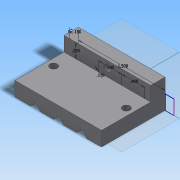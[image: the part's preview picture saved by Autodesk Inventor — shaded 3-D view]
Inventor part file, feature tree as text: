
AUTODESK INVENTOR PART (.ipt)
format: ipt  version: 2014 SP2 (Build 180246200, 246)  size: 177,664 bytes
history: native  units: in
note: dims shown in document units (in); Inventor stores cm internally (conversion verified against a paired STEP export)
features: sketch x6, extrude x6, other x3, hole x2, mirror x1
ambient origin geometry x8: Origin, YZ Plane, XZ Plane, XY Plane, X Axis, Y Axis, Z Axis, Center Point
bodies: Solid1 (feature_tree)
feature tree (18):
  other  "Table"
  other  "keyhole holder-01"
  other  "keyhole holder-02"
  sketch  "Sketch1"  dims[d0=0.1775in d3=0.4in]
  extrude  "Extrusion1"  Depth=0.4in
  extrude  "Extrusion2"  Depth=0.25in
  extrude  "Extrusion3"  Depth=1.1in TaperAngle=0.0deg
  hole  "Hole1"  [1 undecoded]
  mirror  "Mirror1"
  sketch  "Sketch7"  dims[d9=0.81in d10=0.0in d11=0.16in]
  extrude  "Extrusion5"  Depth=0.25in TaperAngle=0.0deg
  hole  "Hole2"  [1 undecoded]
  extrude  "Extrusion6"  Depth=0.25in
  extrude  "Extrusion7"  Depth=0.25in
  sketch  "Sketch2"  dims[d4=0.4in d5=0.25in]
  sketch  "Sketch3"  dims[d6=1.5in d7=1.1in d8=0.0in]
  sketch  "Sketch8"  dims[d12=0.19in d13=0.0in]
  sketch  "Sketch9"  dims[d15=0.129in d16=0.75in d17=0.225in d18=0.188in d19=0.5635in d20=1.0in d21=0.8108in d27=0.25in d28=0.0in d29=0.129in d30=0.75in d31=0.225in d32=0.188in d33=0.5635in d34=1.0in d35=0.8108in d38=0.55in d39=0.63in d40=0.25in d41=0.145in d43=0.1in d44=0.0in d46=0.1in d47=0.0in d48=0.15in d49=0.15in]
note: 2 required parameter values undecoded (feature->parameter linkage not recoverable at this tier; creation-order binding heuristic only, values carry confidence <= 0.55)
